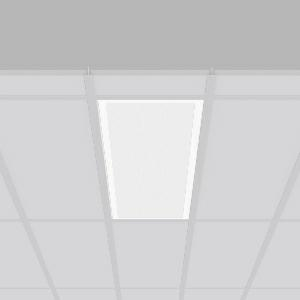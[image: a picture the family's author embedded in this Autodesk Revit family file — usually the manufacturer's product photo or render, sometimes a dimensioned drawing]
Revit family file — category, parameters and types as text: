
# Revit family: sidelite_eco_672375_002_1_07_b018
name_source: partatom
category: Lighting Fixtures
units: mm (PartAtom-declared; Revit-internal decimal feet)

## family parameters
Cut with Voids When Loaded = No
Host = Face
Light Source = No
Part Type = Normal
Room Calculation Point = No
Round Connector Dimension = Use Diameter
Shared = No

## types (1)
- SIDELITE ECO (1 x LED Modul 840, 3500 lm, 4000)
    Apparent Load = 29 VA
    CIE Flux Codes = 59 87 97 100 100
    Color Rendering = 80
    Color Temperature = 4000
    Default Elevation = 1800 mm
    Description = Series: SIDELITE ECO
Highly economical recessed luminaire with progressive LED technology. For escape route illumination. Frame made of aluminium, powder-coated. Diffuser plastic microprismatic. Lightguide and diffuser made of non-yellowing plastic (PMMA). Lateral light emission (RZB SIDELITE technology) for homogeneous light distribution. External driver. Self-contained system with automatic self-test and feedback via DALI bus, only to RZB DALI monitoring system. External driver with simple plug-in locking system. Extended connection cable (1.90 m). 
Colour: white
Length: 1245 mm
Width: 308 mm
Cut-out length: 1220 mm
Cut-out width: 285 mm
Recess height: 160 mm
Luminaire: recess height: 40 mm
Weight: 4.7 kg
Operating mode: maintained power mode
Duration time: 8 h
Lamp: LED
Socket: without socket
Colour temperature: 4000K
Colour rendering index (CRI): 80
System power: 29 W
Rated luminous flux: 3500 lm
Luminous flux, emergency: 240 lm
System power, emergency: -
Control gear: Regulated power supply
Protection class: I
Type of protection: IP 40
    Height = 0 mm  [stored 0 ft]
    Lamp = 1 x LED Modul 840
    Lamp Light Flux = 3500 lm
    Lamp count = 1
    Length = 1245 mm
    Lifetime = 50000 h
    Luminous efficacy = 121 lm/W
    Manufacturer = RZB
    ModVariant = No
    Model = 672375.002.1.07
    Mounting Place = Ceiling
    Mounting Type = Recessed
    Number of Poles = 1
    OnlyDefault = Yes
    Power Factor = 1
    Product Name = SIDELITE ECO
    Product group = Recessed modular luminaires
    ProductGroupID = 406
    Protection Class = Protection class I
    Protection Degree = IP 40
    RLX_Detail_Level = 1
    RLX_Emergency_Light_Flux = 240 lm
    RLX_Emergency_Type = 3
    RLX_Emergency_Type_DB = Yes
    RlxData = <blob elided: 34337 chars, md5=41a797b8>
    Socket = socket
    Standby Power = 0 W
    System Light Flux = 3500 lm
    System Power = 29 W
    Type Comments = Product without accessories
    Type Image = 312368.002.jpg
    URL = http://relux.com
    VarID = ---
    Voltage = 230 V
    Voltage Range = 220-240 V
    Weight = 0.00 kg
    Width = 308 mm

note: [stored X ft] marks values corroborated as IEEE doubles in the binary element streams (Revit-internal decimal feet)

## geometry (parser evidence)
native form markers: Blend x4, Sweep x10
no freeform markers — native parametric forms only
